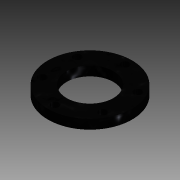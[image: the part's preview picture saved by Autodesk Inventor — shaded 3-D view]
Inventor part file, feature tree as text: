
AUTODESK INVENTOR PART (.ipt)
format: ipt  version: 2014 SP1 (Build 180222100, 222)  size: 97,792 bytes
history: native  units: in
note: dims shown in document units (in); Inventor stores cm internally (conversion verified against a paired STEP export)
features: extrude x2, sketch x2
ambient origin geometry x8: Origin, YZ Plane, XZ Plane, XY Plane, X Axis, Y Axis, Z Axis, Center Point
bodies: Solid1 (feature_tree)
feature tree (4):
  extrude  "Extrusion1"  Depth=1.25in
  extrude  "Extrusion2"  Depth=0.25in
  sketch  "Sketch1"  dims[d0=2.25in d1=1.25in]
  sketch  "Sketch2"  dims[d2=0.25in d3=0.0in d4=1.875in d5=0.204in d6=2.3622in d8=360.0deg d10=1.0in d11=0.0in]
